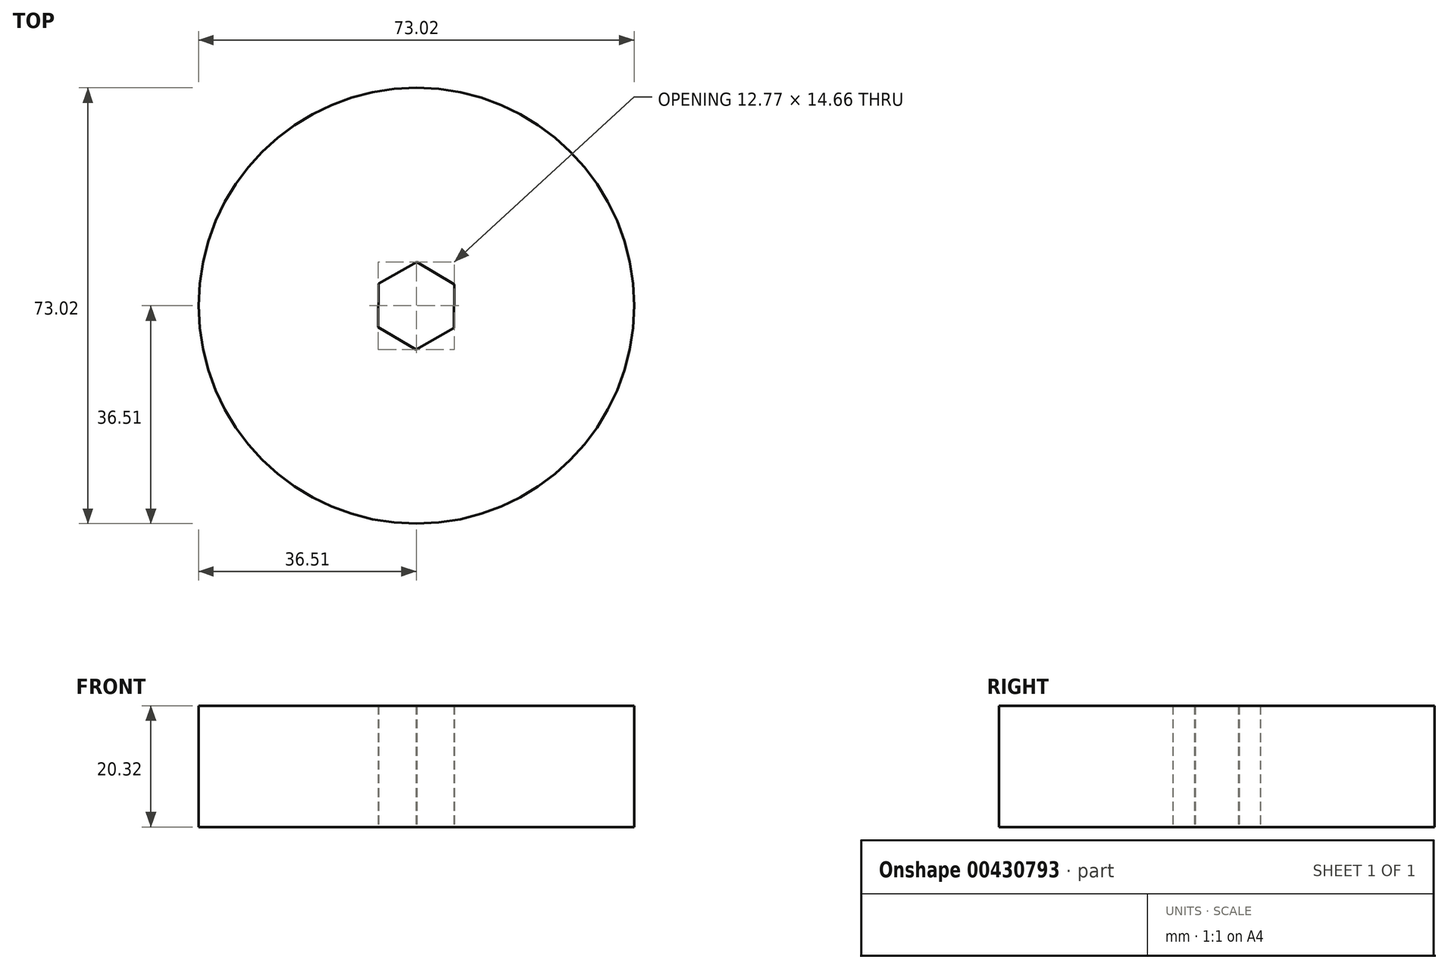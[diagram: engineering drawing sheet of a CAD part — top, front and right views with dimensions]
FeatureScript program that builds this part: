
annotation { "Feature Type Name" : "Feature", "Feature Type Description" : "" }
export const myFeature = defineFeature(function(context is Context, id is Id, definition is map)
    precondition{}
    {
        {
            var Q0;
            Q0=qCreatedBy(makeId("Top.planeOp"),FACE);
            var sketch = newSketch(context, id + "F0", { "sketchPlane" : qUnion([Q0])});
            skCircle(sketch, "E0", {"center": v(0, 0) * mm, "radius": 36.51 * mm});
            skCircle(sketch, "E1.cCircle", {"center": v(0, 0) * mm, "radius": 6.35 * mm, "construction": true});
            skLineSegment(sketch, "E1.0", {"start": v(-6.32, 3.73) * mm, "end": v(0.07, 7.33) * mm});
            skLineSegment(sketch, "E1.1", {"start": v(0.07, 7.33) * mm, "end": v(6.38, 3.6) * mm});
            skLineSegment(sketch, "E1.2", {"start": v(6.38, 3.6) * mm, "end": v(6.32, -3.73) * mm});
            skLineSegment(sketch, "E1.3", {"start": v(6.32, -3.73) * mm, "end": v(-0.07, -7.33) * mm});
            skLineSegment(sketch, "E1.4", {"start": v(-0.07, -7.33) * mm, "end": v(-6.38, -3.6) * mm});
            skLineSegment(sketch, "E1.5", {"start": v(-6.38, -3.6) * mm, "end": v(-6.32, 3.73) * mm});
            skPoint(sketch, "E1.0.midPoint", {"position": v(-3.12, 5.53) * mm});
            skSolve(sketch);
        }
        {
            var Q0;
            Q0 = qSketchRegion(id + "F0", true);
            extrude(context, id + "F1", {"entities" : qUnion([Q0]), "depth" : 20.32 * mm});
        }
    });
